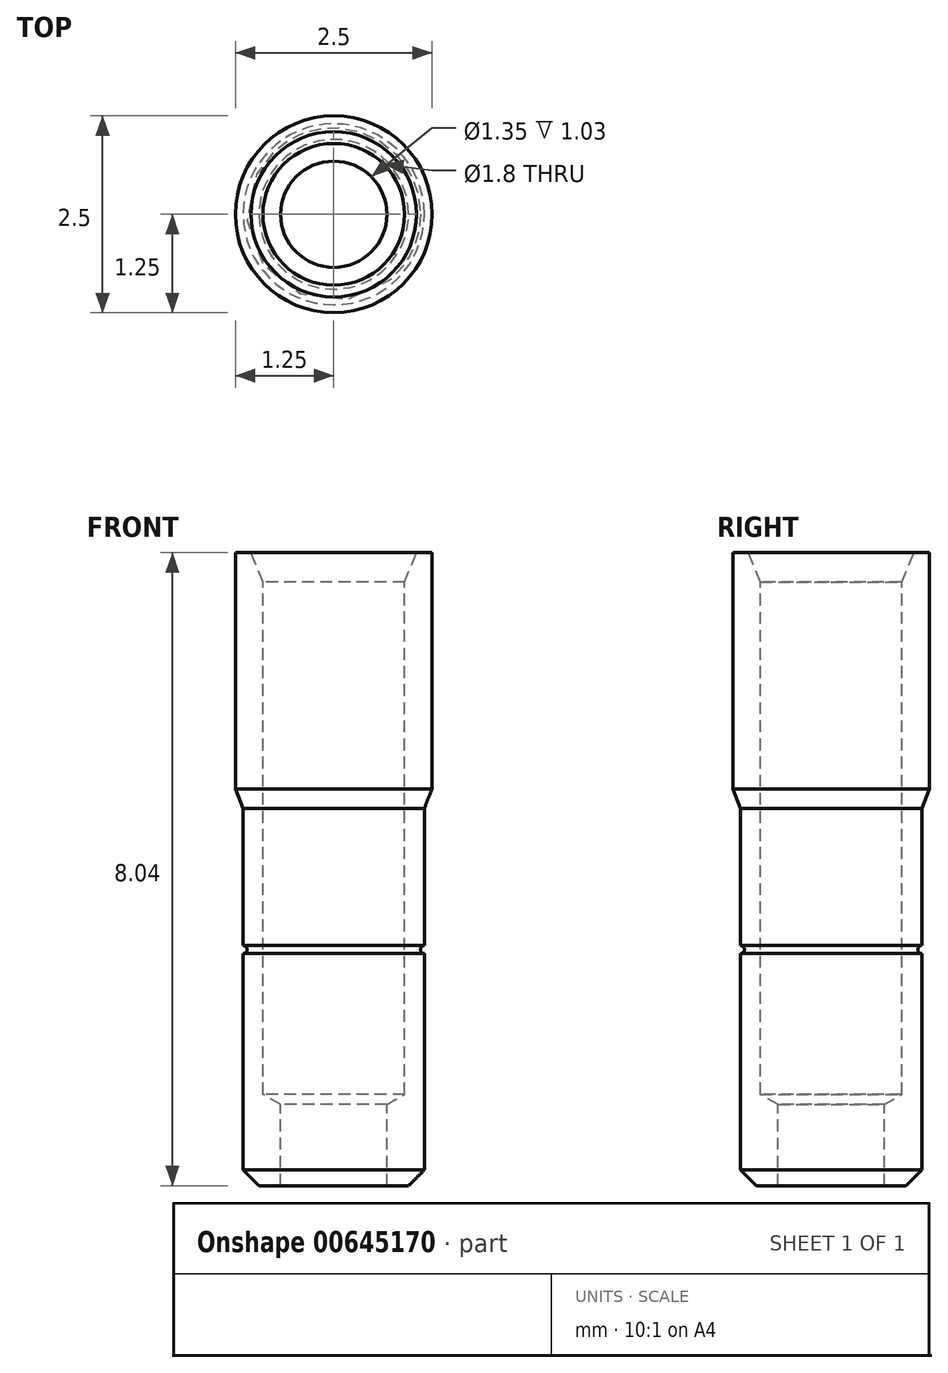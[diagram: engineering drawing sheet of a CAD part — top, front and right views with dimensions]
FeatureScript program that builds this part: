
annotation { "Feature Type Name" : "Feature", "Feature Type Description" : "" }
export const myFeature = defineFeature(function(context is Context, id is Id, definition is map)
    precondition{}
    {
        {
            var Q0;
            Q0=qCreatedBy(makeId("Front.planeOp"),FACE);
            var sketch = newSketch(context, id + "F0", { "sketchPlane" : qUnion([Q0])});
            skLineSegment(sketch, "E0", {"start": v(-1.05, 8.04) * mm, "end": v(-1.25, 8.04) * mm});
            skLineSegment(sketch, "E1", {"start": v(-1.25, 8.04) * mm, "end": v(-1.25, 5.04) * mm});
            skLineSegment(sketch, "E2", {"start": v(-1.25, 5.04) * mm, "end": v(-1.15, 4.8) * mm});
            skLineSegment(sketch, "E3", {"start": v(-1.15, 4.8) * mm, "end": v(-1.15, 3.05) * mm});
            skLineSegment(sketch, "E4", {"start": v(0, 5.35) * mm, "end": v(0, -0.22) * mm, "construction": true});
            skLineSegment(sketch, "E5", {"start": v(-1.05, 8.04) * mm, "end": v(-0.9, 7.67) * mm});
            skLineSegment(sketch, "E6", {"start": v(-0.9, 7.67) * mm, "end": v(-0.9, 1.16) * mm});
            skLineSegment(sketch, "E7", {"start": v(-0.9, 1.16) * mm, "end": v(-0.67, 1.03) * mm});
            skLineSegment(sketch, "E8", {"start": v(-0.67, 1.03) * mm, "end": v(-0.67, 0) * mm});
            skLineSegment(sketch, "E9", {"start": v(-0.67, 0) * mm, "end": v(-0.95, 0) * mm});
            skLineSegment(sketch, "E10", {"start": v(-0.95, 0) * mm, "end": v(-1.15, 0.2) * mm});
            skPoint(sketch, "E11.orphan", {"position": v(-1.15, 0) * mm});
            skArc(sketch, "E12", {"start": v(-1.15, 2.95) * mm, "mid": v(-1.1, 3) * mm, "end": v(-1.15, 3.05) * mm});
            skLineSegment(sketch, "E13.trimOffspring", {"start": v(-1.15, 2.95) * mm, "end": v(-1.15, 0.2) * mm});
            skSolve(sketch);
        }
        {
            var Q0;
            Q0=makeQuery(id+"F0.imprint","IMPRINT",FACE,{"disambiguationData":[TD([[makeQuery(id+"F0.imprint","IMPRINT",EDGE,{"derivedFrom":sQuery(id+"F0.wireOp",EDGE,"E0")}),1.0]])]});
            var Q1;
            Q1=sQuery(id+"F0.wireOp",EDGE,"E4");
            revolve(context, id + "F1", {"entities" : qUnion([Q0]), "axis" : qUnion([Q1]), "revolveType" : RevolveType.FULL});
        }
    });
